# Revit family: ElectricalFixture_WiringAccessories_Hager_Sollysta_20ADoublePoleSwitches
name_source: partatom
category: Electrical Fixtures
revit_build: Autodesk Revit 2015 (Build: 20160512_1515(x64)
units: mm (PartAtom-declared; Revit-internal decimal feet)

## types (27) — shared parameters
CE Approval = Yes
Colour = SollystaWhite
Design Country = China
Expected Life = 25 years
Extrusion From Wall = 11.9 mm
Finish = Gloss
Frequency = 50/60Hz
Gross Weight kg = 0.165
Manufacturer = Hager
Manufacturer Country = United Kingdom
Manufacturer Website = http://www.hager.co.uk
Material = Urea Formaldehyde Thermoset Plastic
Overall Depth = 26.1 mm
Overall Height = 86 mm  [stored 0.282152 ft]
Overall Length = 86 mm  [stored 0.282152 ft]
Packaging Recyclable = Yes
Product Family = WhiteMouldedSockets_20APoleSwitches
Product Group = WiringAccessories
Product Literature = http://www.hager.co.uk
Product Range = Sollysta
Product URL = http://www.hager.co.uk
Reference Standard = BS 1363-2
Shape = Rectangular
Shipping Weight kg = 0.188
Supply Phase = 1
Type = ElectricalFixture
Voltage (Volts) = 230V/240V
zero-valued in all types: Overall Width

## per-type parameters (varying)
| type | Default Elevation | Description | EAN Code | Features | Flex Outlet | LED Indicator Switch | Name | Switch | Technical Description |
| WMDP84 | 1219.2 mm  [stored 4 ft] | 20ADoublePoleSwitch | 5015652260370 | 20ADoublePoleSwitch | No | No | WhiteMouldedSocket_WMDP84 | Yes | 20ADoublePoleSwitch |
| WMDP84FO | 1219.2 mm  [stored 4 ft] | 20ADoublePoleSwitchWithFlexOutlet | 5015652260387 | 20ADoublePoleSwitchWithFlexOutlet | Yes | No | WhiteMoldedSocket_WMSS82 | Yes | 20ADoublePoleSwitchWithFlexOutlet |
| WMDP84N | 300 mm | 20ADoublePoleSwitchWithLEDIndicator | 5015652260516 | 20ADoublePoleSwitchWithLEDIndicator | No | Yes | WhiteMouldedSocket_WMSS82 | No | 20ADoublePoleSwitchWithLEDIndicator |
| WMDP84FON | 300 mm | 20ADoublePoleSwitchWithLEDIndicatorAndFlexOutlet | 5015652260523 | 20ADoublePoleSwitchWithLEDIndicatorAndFlexOutlet | Yes | Yes | WhiteMoldedSocket_WMDP84FON | No | 20ADoublePoleSwitchWithLEDIndicatorAndFlexOutlet |
| WMDP85N | 300 mm | 20ADoublePoleSwitchWithLEDIndicatorMarkedWaterheater | 5015652260653 | 20ADoublePoleSwitchWithLEDIndicatorMarkedWaterheater | No | Yes | WhiteMouldedSocket_WMDP85N | No | 20ADoublePoleSwitchWithLEDIndicatorMarkedWaterheater |
| WMDP84DW | 1219.2 mm  [stored 4 ft] | 20ADPSwitchMkdDishwasher | 5015654760151 | 20ADPSwitchMkdDishwasher | No | No | WhiteMouldedSocket_WMDP84DW | Yes | 20ADPSwitchMkdDishwasher |
| WMDP84/FRE | 1219.2 mm  [stored 4 ft] | 20ADoublePoleSwitchMarkedFreezer | 5015652260394 | 20ADoublePoleSwitchMarkedFreezer | No | No | WhiteMouldedSocket_WMDP84/FRE | Yes | 20ADoublePoleSwitchMarkedFreezer |
| WMDP84/FRI | 1219.2 mm  [stored 4 ft] | 20ADoublePoleSwitchMarkedFridge | 5015652260417 | 20ADoublePoleSwitchMarkedFridge | No | No | WhiteMouldedSocket_WMDP84/FRI | Yes | 20ADoublePoleSwitchMarkedFridge |
| WMDP84/TD | 1219.2 mm  [stored 4 ft] | 20ADoublePoleSwitchMarkedTumbleDryer | 5015652260431 | 20ADoublePoleSwitchMarkedTumbleDryer | No | No | WhiteMouldedSocket_WMDP84/TD | Yes | 20ADoublePoleSwitchMarkedTumbleDryer |
| WMDP84/WM | 1219.2 mm  [stored 4 ft] | 20ADoublePoleSwitchMarkedWashingMachine | 5015652260455 | 20ADoublePoleSwitchMarkedWashingMachine | No | No | WhiteMouldedSocket_WMDP84/WM | Yes | 20ADoublePoleSwitchMarkedWashingMachine |
| WMDP85FON | 300 mm | 20ADoublePoleSwitchWithLEDIndicatorAndFlexOutletMarkedWaterheater | 5015652260660 | 20ADoublePoleSwitchWithLEDIndicatorAndFlexOutletMarkedWaterheater | Yes | Yes | WhiteMouldedSocket_WMDP85FON | No | 20ADoublePoleSwitchWithLEDIndicatorAndFlexOutletMarkedWaterheater |
| WMDP84FO/FRE | 1219.2 mm  [stored 4 ft] | 20ADoublePoleSwitchWithFlexOutletMarkedFreezer | 5015652260400
5015652260400 | 20ADoublePoleSwitchWithFlexOutletMarkedFreezer | Yes | No | WhiteMouldedSocket_WMDP84FO/FRE | Yes | 20ADoublePoleSwitchWithFlexOutletMarkedFreezer |
| WMDP84FO/FRI | 1219.2 mm  [stored 4 ft] | 20ADoublePoleSwitchWithFlexOutletMarkedFridge | 5015652260424 | 20ADoublePoleSwitchWithFlexOutletMarkedFridge | Yes | No | WhiteMouldedSocket_WMDP84FO/FRI | Yes | 20ADoublePoleSwitchWithFlexOutletMarkedFridge |
| WMDP84FO/TD | 1219.2 mm  [stored 4 ft] | 20ADoublePoleSwitchWithFlexOutletMarkedTumbleDryer | 5015652260448 | 20ADoublePoleSwitchWithFlexOutletMarkedTumbleDryer | Yes | No | WhiteMouldedSocket_WMDP84FO/TD | Yes | 20ADoublePoleSwitchWithFlexOutletMarkedTumbleDryer |
| WMDP84FO/WM | 1219.2 mm  [stored 4 ft] | 20ADoublePoleSwitchWithFlexOutletMarkedWashingMachine | 5015652260462 | 20ADoublePoleSwitchWithFlexOutletMarkedWashingMachine | Yes | No | WhiteMouldedSocket_WMDP84FO/WM | Yes | 20ADoublePoleSwitchWithFlexOutletMarkedWashingMachine |
| WMDP84FON/DW | 1219.2 mm  [stored 4 ft] | 20ADoublePoleSwitchWithLEDIndicator&FlexOutletMarkedDishwasher | 5015652260547 | 20ADoublePoleSwitchWithLEDIndicator&FlexOutletMarkedDishwasher | Yes | Yes | WhiteMouldedSocket_WMDP84FO/DW | No | 20ADoublePoleSwitchWithLEDIndicator&FlexOutletMarkedDishwasher |
| WMDP84FON/FAN | 1219.2 mm  [stored 4 ft] | 20ADoublePoleSwitchWithLEDIndicator&FlexOutletMarkedFan | 5015652260561 | 20ADoublePoleSwitchWithLEDIndicator&FlexOutletMarkedFan | Yes | Yes | WhiteMouldedSocket_WMDP84FON/FAN | No | 20ADoublePoleSwitchWithLEDIndicator&FlexOutletMarkedFan |
| WMDP84FON/FRE | 1219.2 mm  [stored 4 ft] | 20ADoublePoleSwitchWithLEDIndicator&FlexOutletMarkedFreezer | 5015652260585 | 20ADoublePoleSwitchWithLEDIndicator&FlexOutletMarkedFreezer | Yes | Yes | WhiteMouldedSocket_WMDP84FON/FRE | No | 20ADoublePoleSwitchWithLEDIndicator&FlexOutletMarkedFreezer |
| WMDP84FON/FRI | 1219.2 mm  [stored 4 ft] | 20ADoublePoleSwitchWithLEDIndicator&FlexOutletMarkedFridge | 5015652260608 | 20ADoublePoleSwitchWithLEDIndicator&FlexOutletMarkedFridge | Yes | Yes | WhiteMouldedSocket_WMDP84FON/FRI | No | 20ADoublePoleSwitchWithLEDIndicator&FlexOutletMarkedFridge |
| WMDP84FON/TD | 1219.2 mm  [stored 4 ft] | 20ADoublePoleSwitchWithLEDIndicator&FlexOutletMarkedTumbleDryer | 5015652260622 | 20ADoublePoleSwitchWithLEDIndicator&FlexOutletMarkedTumbleDryer | Yes | Yes | WhiteMouldedSocket_WMDP84FON/TD | No | 20ADoublePoleSwitchWithLEDIndicator&FlexOutletMarkedTumbleDryer |
| WMDP84FON/WM | 1219.2 mm  [stored 4 ft] | 20ADoublePoleSwitchWithLEDIndicator&FlexOutletMarkedWashingMachine | 5015652260646 | 20ADoublePoleSwitchWithLEDIndicator&FlexOutletMarkedWashingMachine | Yes | Yes | WhiteMouldedSocket_WMDP84FON/WM | No | 20ADoublePoleSwitchWithLEDIndicator&FlexOutletMarkedWashingMachine |
| WMDP84N/DW | 1219.2 mm  [stored 4 ft] | 20ADoublePoleSwitchWithLEDIndicatorMarkedDishwasher | 5015652260530 | 20ADoublePoleSwitchWithLEDIndicatorMarkedDishwasher | No | Yes | WhiteMouldedSocket_WMDP84FON/WM | No | 20ADoublePoleSwitchWithLEDIndicatorMarkedDishwasher |
| WMDP84N/FAN | 1219.2 mm  [stored 4 ft] | 20ADoublePoleSwitchWithLEDIndicatorMarkedFan | 5015652260554 | 20ADoublePoleSwitchWithLEDIndicatorMarkedFan | No | Yes | WhiteMouldedSocket_WMDP84N/FAN | No | 20ADoublePoleSwitchWithLEDIndicatorMarkedFan |
| WMDP84N/FRE | 1219.2 mm  [stored 4 ft] | 20ADoublePoleSwitchWithLEDIndicatorMarkedFreezer | 5015652260578 | 20ADoublePoleSwitchWithLEDIndicatorMarkedFreezer | No | Yes | WhiteMouldedSocket_WMDP84N/FRE | No | 20ADoublePoleSwitchWithLEDIndicatorMarkedFreezer |
| WMDP84N/FRI | 1219.2 mm  [stored 4 ft] | 20ADoublePoleSwitchWithLEDIndicatorMarkedFridge | 5015652260592 | 20ADoublePoleSwitchWithLEDIndicatorMarkedFridge | No | Yes | WhiteMouldedSocket_WMDP84N/FRI | No | 20ADoublePoleSwitchWithLEDIndicatorMarkedFridge |
| WMDP84N/TD | 1219.2 mm  [stored 4 ft] | 20ADoublePoleSwitchWithLEDIndicatorMarkedTumbledryer | 5015652260615 | 20ADoublePoleSwitchWithLEDIndicatorMarkedTumbledryer | No | Yes | WhiteMouldedSocket_WMDP84N/TD | No | 20ADoublePoleSwitchWithLEDIndicatorMarkedTumbledryer |
| WMDP84N/WM | 1219.2 mm  [stored 4 ft] | 20ADoublePoleSwitchWithLEDIndicatorMarkedWashingMachine | 5015652260639 | 20ADoublePoleSwitchWithLEDIndicatorMarkedWashingMachine | No | Yes | WhiteMouldedSocket_WMDP84N/WM | No | 20ADoublePoleSwitchWithLEDIndicatorMarkedWashingMachine |

note: column(s) folded — value = type name in every type: Product Model Number, Unique Reference

note: [stored X ft] marks values corroborated as IEEE doubles in the binary element streams (Revit-internal decimal feet)

## geometry (parser evidence)
native form markers: Blend x4, Sweep x2
no freeform markers — native parametric forms only
